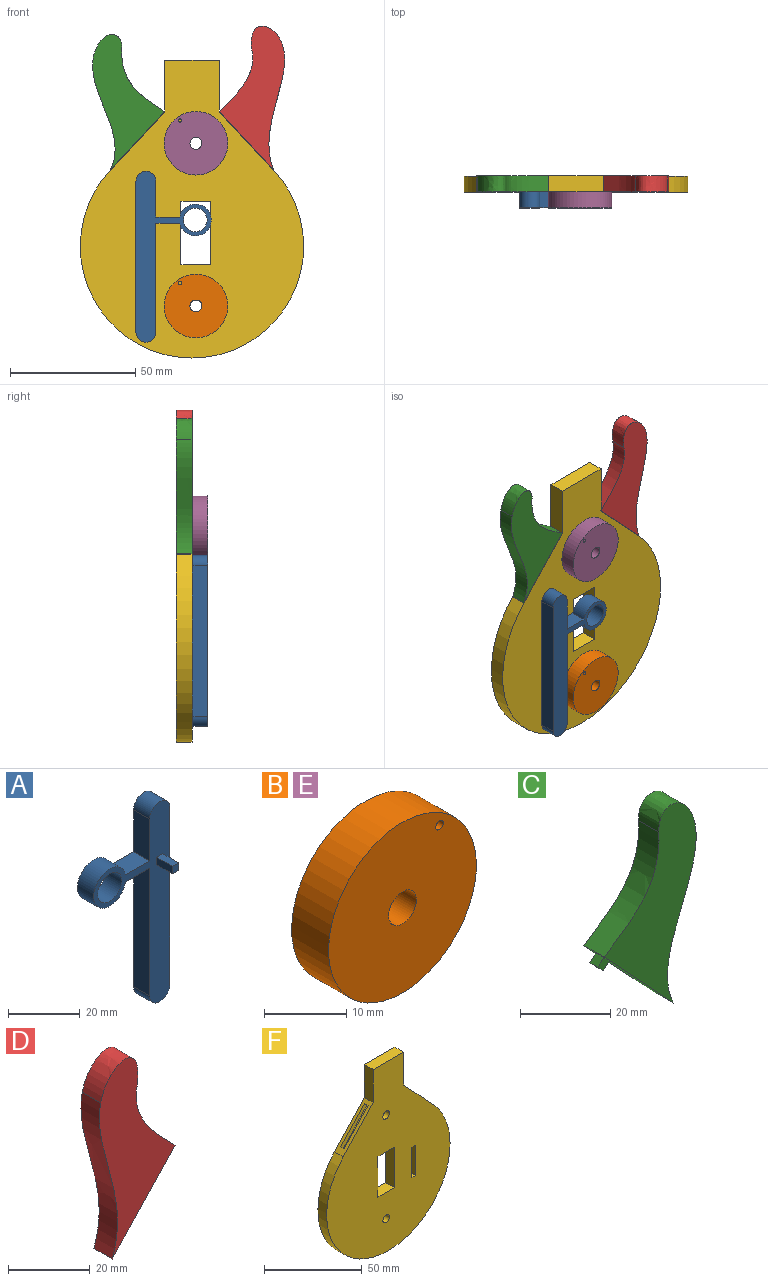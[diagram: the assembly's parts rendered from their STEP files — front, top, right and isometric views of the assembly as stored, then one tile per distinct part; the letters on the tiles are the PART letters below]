
ASSEMBLY  parts=6 mates=5
PART A: 16 faces, bbox 30x12.6x68.3 mm
  f0: plane 14.29x6.35mm, normal (-1,0,0), area 90.7mm2, adj f1,f7,f9,f10
  f1: plane 9.51x6.35mm, normal (0,0,1), area 60.4mm2, adj f0,f2,f9,f10
  f2: cylinder r=6.35mm len=12.7mm, axis (0,1,0), area 237.6mm2, adj f1,f3,f9,f10
  f3: plane 9.53x6.35mm, normal (0,0,-1), area 60.5mm2, adj f2,f4,f9,f10
  f4: plane 43.57x6.35mm, normal (-1,0,0), area 276.7mm2, adj f3,f5,f9,f10
  f5: cylinder r=3.97mm len=7.94mm, axis (0,1,0), area 79.2mm2, adj f4,f6,f9,f10
  f6: plane 60.33x6.35mm, normal (1,0,0), area 383.1mm2, adj f5,f7,f9,f10
  f7: cylinder r=3.97mm len=7.94mm, axis (0,1,0), area 79.2mm2, adj f0,f6,f9,f10
  f8: cylinder r=4.7mm len=9.4mm, axis (0,1,0), area 187.6mm2, adj f9,f10
  f9: plane 68.26x30.04mm, normal (0,-1,0), area 602.7mm2, adj f0,f1,f2,f3,f4,f5,f6,f7
  f10: plane 68.26x30.04mm, normal (0,1,0), area 608.8mm2, adj f0,f1,f2,f3,f4,f5,f6,f7
  f11: plane 6.22x2.41mm, normal (0,0,-1), area 15mm2, adj f9,f12,f14,f15
  f12: plane 6.22x2.54mm, normal (-1,0,0), area 15.8mm2, adj f9,f11,f13,f15
  f13: plane 6.22x2.41mm, normal (0,0,1), area 15mm2, adj f9,f12,f14,f15
  f14: plane 6.22x2.54mm, normal (1,0,0), area 15.8mm2, adj f9,f11,f13,f15
  f15: plane 2.54x2.41mm, normal (0,-1,0), area 6.1mm2, adj f11,f12,f13,f14
PART B: 5 faces, bbox 25.4x6.4x25.4 mm
  f0: cylinder r=2.39mm len=6.35mm, axis (0,1,0), area 95.3mm2, adj f3,f4
  f1: cylinder r=0.65mm len=6.35mm, axis (0,1,0), area 25.9mm2, adj f3,f4
  f2: cylinder r=12.7mm len=25.4mm, axis (0,1,0), area 506.7mm2, adj f3,f4
  f3: plane 25.4x25.4mm, normal (0,-1,0), area 487.5mm2, adj f0,f1,f2
  f4: plane 25.4x25.4mm, normal (0,1,0), area 487.5mm2, adj f0,f1,f2
PART C: 11 faces, bbox 30.7x6.4x55.6 mm
  f0: plane 23.22x21.65mm, normal (-0.73,0,-0.68), area 195.3mm2, adj f1,f3,f4,f5,f6,f7,f8,f9
  f1: extruded ~45.61x8.95mm, area 300.4mm2, adj f0,f2,f4,f5
  f2: extruded ~11.29x8.5mm, area 124.8mm2, adj f1,f3,f4,f5
  f3: extruded ~25.38x17.18mm, area 207mm2, adj f0,f2,f4,f5
  f4: plane 55.56x30.64mm, normal (0,-1,0), area 653.1mm2, adj f0,f1,f2,f3
  f5: plane 55.56x30.64mm, normal (0,1,0), area 653.1mm2, adj f0,f1,f2,f3
  f6: plane 3.59x3.59mm, normal (0,-1,0), area 6.5mm2, adj f0,f7,f9,f10
  f7: plane 2.49x1.86mm, normal (-0.68,0,0.73), area 6.3mm2, adj f0,f6,f8,f10
  f8: plane 3.59x3.59mm, normal (0,1,0), area 6.5mm2, adj f0,f7,f9,f10
  f9: plane 2.49x1.86mm, normal (0.68,0,-0.73), area 6.3mm2, adj f0,f6,f8,f10
  f10: plane 2.49x1.86mm, normal (-0.73,0,-0.68), area 6.3mm2, adj f6,f7,f8,f9
PART D: 11 faces, bbox 27.7x6.4x59.9 mm
  f0: extruded ~48.63x6.35mm, area 314.7mm2, adj f1,f3,f4,f5
  f1: plane 23.22x21.65mm, normal (0.73,0,-0.68), area 195.2mm2, adj f0,f2,f4,f5,f6,f7,f8,f9
  f2: extruded ~24.49x13.39mm, area 184.4mm2, adj f1,f3,f4,f5
  f3: extruded ~12.86x9.78mm, area 159.7mm2, adj f0,f2,f4,f5
  f4: plane 59.88x27.67mm, normal (0,-1,0), area 699.5mm2, adj f0,f1,f2,f3
  f5: plane 59.88x27.67mm, normal (0,1,0), area 699.5mm2, adj f0,f1,f2,f3
  f6: plane 3.59x3.59mm, normal (0,1,0), area 6.5mm2, adj f1,f7,f9,f10
  f7: plane 2.51x1.86mm, normal (0.68,0,0.73), area 6.4mm2, adj f1,f6,f8,f10
  f8: plane 3.59x3.59mm, normal (0,-1,0), area 6.5mm2, adj f1,f7,f9,f10
  f9: plane 2.51x1.86mm, normal (-0.68,0,-0.73), area 6.4mm2, adj f1,f6,f8,f10
  f10: plane 2.51x1.86mm, normal (0.73,0,-0.68), area 6.4mm2, adj f6,f7,f8,f9
PART E: same geometry as B
PART F: 28 faces, bbox 89.2x6.4x118.9 mm
  f0: plane 23.22x21.65mm, normal (0.73,0,0.68), area 137.1mm2, adj f2,f3,f16,f17,f23,f24,f25,f26
  f1: plane 23.22x21.65mm, normal (-0.73,0,0.68), area 137.1mm2, adj f2,f15,f16,f17,f18,f19,f20,f21
  f2: cylinder r=44.61mm len=89.22mm, axis (0,1,0), area 1315mm2, adj f0,f1,f16,f17
  f3: plane 20.64x6.35mm, normal (1,0,0), area 131mm2, adj f0,f4,f16,f17
  f4: plane 21.95x6.35mm, normal (0,0,1), area 139.4mm2, adj f3,f15,f16,f17
  f5: plane 18.9x6.35mm, normal (1,0,0), area 120mm2, adj f6,f11,f16,f17
  f6: plane 6.35x2.79mm, normal (0,0,-1), area 17.7mm2, adj f5,f7,f16,f17
  f7: plane 18.9x6.35mm, normal (-1,0,0), area 120mm2, adj f6,f11,f16,f17
  f8: plane 11.96x6.35mm, normal (0,0,-1), area 76mm2, adj f9,f14,f16,f17
  f9: plane 25.4x6.35mm, normal (-1,0,0), area 161.3mm2, adj f8,f10,f16,f17
  f10: plane 11.96x6.35mm, normal (0,0,1), area 76mm2, adj f9,f14,f16,f17
  f11: plane 6.35x2.79mm, normal (0,0,1), area 17.7mm2, adj f5,f7,f16,f17
  f12: cylinder r=2.39mm len=6.35mm, axis (0,1,0), area 95.3mm2, adj f16,f17
  f13: cylinder r=2.39mm len=6.35mm, axis (0,1,0), area 95.3mm2, adj f16,f17
  f14: plane 25.4x6.35mm, normal (1,0,0), area 161.3mm2, adj f8,f10,f16,f17
  f15: plane 20.64x6.35mm, normal (-1,0,0), area 131mm2, adj f1,f4,f16,f17
  f16: plane 118.89x89.22mm, normal (0,-1,0), area 6684.7mm2, adj f0,f1,f2,f3,f4,f5,f6,f7
  f17: plane 118.89x89.22mm, normal (0,1,0), area 6684.7mm2, adj f0,f1,f2,f3,f4,f5,f6,f7
  f18: plane 2.54x1.86mm, normal (-0.68,0,-0.73), area 6.5mm2, adj f1,f19,f21,f22
  f19: plane 20.31x19.18mm, normal (0,-1,0), area 64.5mm2, adj f1,f18,f20,f22
  f20: plane 2.54x1.86mm, normal (0.68,0,0.73), area 6.5mm2, adj f1,f19,f21,f22
  f21: plane 20.31x19.18mm, normal (0,1,0), area 64.5mm2, adj f1,f18,f20,f22
  f22: plane 18.58x17.32mm, normal (-0.73,0,0.68), area 64.5mm2, adj f18,f19,f20,f21
  f23: plane 2.54x1.86mm, normal (0.68,0,-0.73), area 6.5mm2, adj f0,f24,f26,f27
  f24: plane 20.31x19.18mm, normal (0,1,0), area 64.5mm2, adj f0,f23,f25,f27
  f25: plane 2.54x1.86mm, normal (-0.68,0,0.73), area 6.5mm2, adj f0,f24,f26,f27
  f26: plane 20.31x19.18mm, normal (0,-1,0), area 64.5mm2, adj f0,f23,f25,f27
  f27: plane 18.58x17.32mm, normal (0.73,0,0.68), area 64.5mm2, adj f23,f24,f25,f26
PLACE A rot(axis=(0,0,1),180deg) t=(-38.76,-25.2,-28.15)mm
PLACE B rot(axis=(0,0,1),180deg) t=(-18.79,-25.27,-47.81)mm
PLACE C rot(axis=(0,0,1),180deg) t=(-18.71,-18.92,6.53)mm
PLACE D rot(axis=(0,0,1),180deg) t=(-18.87,-18.92,6.53)mm
PLACE E rot(axis=(0,0,1),180deg) t=(-18.79,-25.27,17.18)mm
PLACE F rot(axis=(0,0,1),180deg) t=(-18.79,-18.92,6.44)mm fixed
MATE revolute B.f0 <-> F.f13  axis (0,1,0) through (-18.79,-22.09,-47.81)mm
MATE pin_slot F.f1 <-> D.f1  axis (0.73,0,0.68) through (1.62,-18.92,17.85)mm
MATE revolute F.f12 <-> E.f2  axis (0,-1,0) through (-18.79,-22.09,17.18)mm
MATE pin_slot F.f0 <-> C.f0  axis (-0.73,0,0.68) through (-42.35,-18.92,17.85)mm
MATE slider F.f6 <-> A.f13  axis (0,0,-1) through (-38.76,-18.92,-12.4)mm
